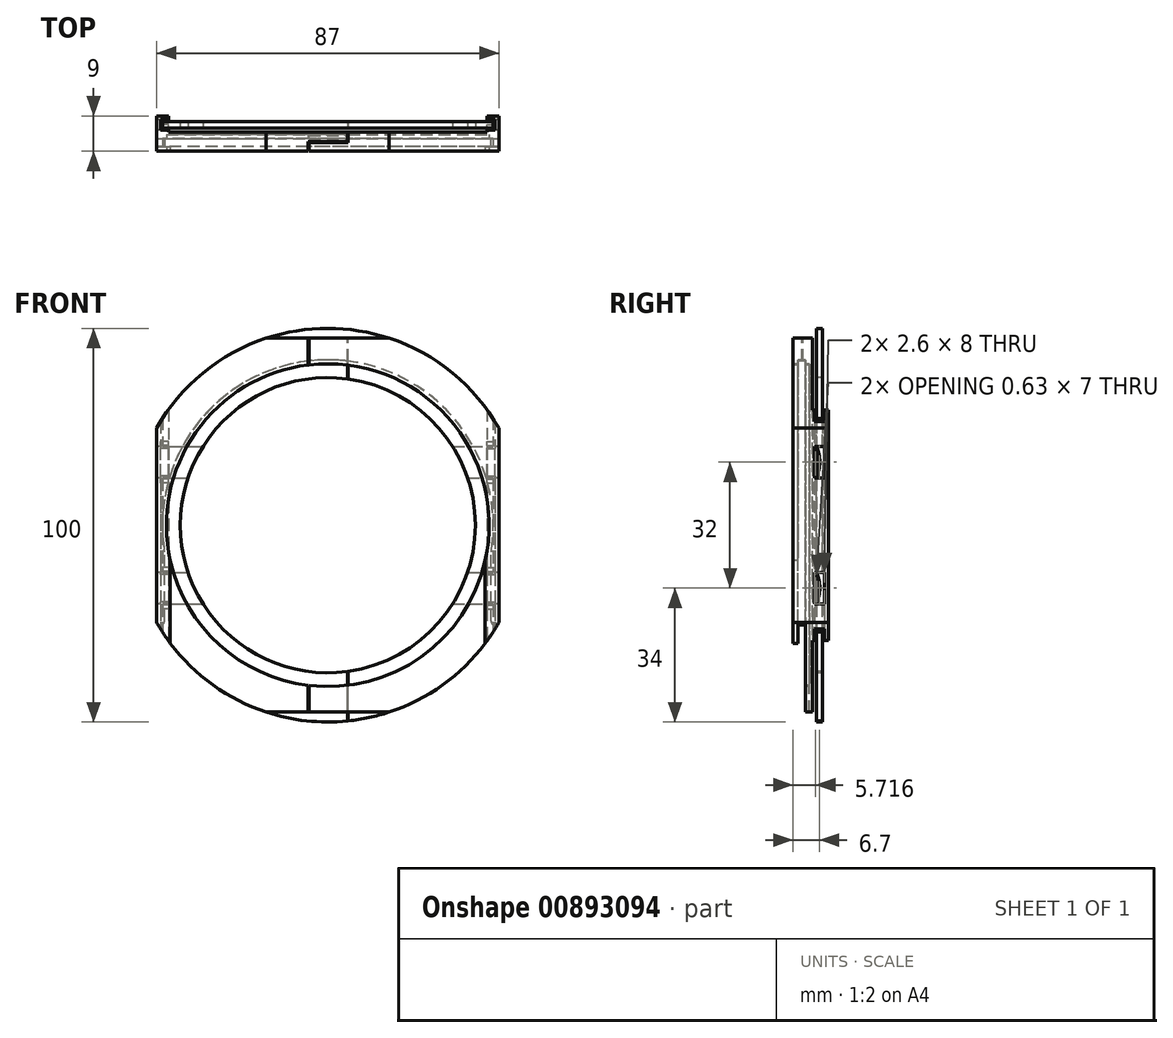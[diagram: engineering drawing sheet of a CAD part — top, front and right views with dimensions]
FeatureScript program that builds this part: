
annotation { "Feature Type Name" : "Feature", "Feature Type Description" : "" }
export const myFeature = defineFeature(function(context is Context, id is Id, definition is map)
    precondition{}
    {
        {
            var Q0;
            Q0=qCreatedBy(makeId("Front.planeOp"),FACE);
            var sketch = newSketch(context, id + "F0", { "sketchPlane" : qUnion([Q0])});
            skLineSegment(sketch, "E0.bottom", {"start": v(42, 50) * mm, "end": v(-42, 50) * mm});
            skLineSegment(sketch, "E0.top", {"start": v(42, -50) * mm, "end": v(-42, -50) * mm});
            skLineSegment(sketch, "E0.left", {"start": v(42, 50) * mm, "end": v(42, -50) * mm});
            skLineSegment(sketch, "E0.right", {"start": v(-42, 50) * mm, "end": v(-42, -50) * mm});
            skPoint(sketch, "E0.middle", {"position": v(0, 0) * mm});
            skSolve(sketch);
        }
        {
            var Q0;
            Q0=makeQuery(id+"F0.imprint","IMPRINT",FACE,{"disambiguationData":[TD([[makeQuery(id+"F0.imprint","IMPRINT",EDGE,{"derivedFrom":sQuery(id+"F0.wireOp",EDGE,"E0.bottom")}),1.0]])]});
            extrude(context, id + "F1", {"entities" : qUnion([Q0]), "depth" : .8 * mm, "offsetDistance" : 25 * mm, "hasSecondDirection" : true, "secondDirectionOppositeDirection" : true, "secondDirectionDepth" : .8 * mm});
        }
        {
            var Q0;
            Q0=qCreatedBy(makeId("Top.planeOp"),FACE);
            var sketch = newSketch(context, id + "F2", { "sketchPlane" : qUnion([Q0])});
            skLineSegment(sketch, "E1.0", {"start": v(42, 0.8) * mm, "end": v(-42, 0.8) * mm, "construction": true});
            skLineSegment(sketch, "E2.0", {"start": v(-42, -0.8) * mm, "end": v(-42, 0.8) * mm, "construction": true});
            skLineSegment(sketch, "E3.0", {"start": v(42, -0.8) * mm, "end": v(-42, -0.8) * mm, "construction": true});
            skLineSegment(sketch, "E4.0", {"start": v(42, -0.8) * mm, "end": v(42, 0.8) * mm, "construction": true});
            skLineSegment(sketch, "E5", {"start": v(-42.5, 1.3) * mm, "end": v(-42.5, -1.3) * mm});
            skLineSegment(sketch, "E6", {"start": v(-42.5, 1.3) * mm, "end": v(-40.5, 1.3) * mm});
            skLineSegment(sketch, "E7.MirrorCS", {"start": v(42.5, 1.3) * mm, "end": v(42.5, -1.3) * mm});
            skLineSegment(sketch, "E8.MirrorCS", {"start": v(42.5, 1.3) * mm, "end": v(40.5, 1.3) * mm});
            skLineSegment(sketch, "E9", {"start": v(-40.5, 1.3) * mm, "end": v(-40.5, 2.3) * mm});
            skLineSegment(sketch, "E10", {"start": v(-40.5, 2.3) * mm, "end": v(-43.5, 2.3) * mm});
            skLineSegment(sketch, "E11", {"start": v(-43.5, 2.3) * mm, "end": v(-43.5, -6.7) * mm});
            skLineSegment(sketch, "E12.MirrorCS", {"start": v(40.5, 1.3) * mm, "end": v(40.5, 2.3) * mm});
            skLineSegment(sketch, "E13.MirrorCS", {"start": v(40.5, 2.3) * mm, "end": v(43.5, 2.3) * mm});
            skLineSegment(sketch, "E14.MirrorCS", {"start": v(43.5, 2.3) * mm, "end": v(43.5, -6.7) * mm});
            skLineSegment(sketch, "E15", {"start": v(-43.5, -6.7) * mm, "end": v(43.5, -6.7) * mm});
            skLineSegment(sketch, "E16", {"start": v(-42.5, -1.3) * mm, "end": v(-40.5, -1.3) * mm});
            skLineSegment(sketch, "E17", {"start": v(-40.5, -1.3) * mm, "end": v(-40.5, -1.8) * mm});
            skLineSegment(sketch, "E18.MirrorCS", {"start": v(42.5, -1.3) * mm, "end": v(40.5, -1.3) * mm});
            skLineSegment(sketch, "E19.MirrorCS", {"start": v(40.5, -1.3) * mm, "end": v(40.5, -1.8) * mm});
            skLineSegment(sketch, "E20", {"start": v(40.5, -1.8) * mm, "end": v(-40.5, -1.8) * mm});
            skSolve(sketch);
        }
        {
            var Q0;
            Q0=qSketchRegion(id+"F2",true);
            extrude(context, id + "F3", {"entities" : qUnion([Q0]), "endBound" : BoundingType.SYMMETRIC, "depth" : 95 * mm, "offsetDistance" : 25 * mm});
        }
        {
            var Q0;
            Q0=qCreatedBy(makeId("Right.planeOp"),FACE);
            var sketch = newSketch(context, id + "F4", { "sketchPlane" : qUnion([Q0])});
            skLineSegment(sketch, "E21.top", {"start": v(3, 37.5) * mm, "end": v(-2.5, 37.5) * mm});
            skLineSegment(sketch, "E22", {"start": v(-2.5, 37.5) * mm, "end": v(-2.5, 41) * mm});
            skLineSegment(sketch, "E23", {"start": v(-2.5, 41) * mm, "end": v(-3.5, 41) * mm});
            skLineSegment(sketch, "E24", {"start": v(-3.5, 41) * mm, "end": v(-3.5, 42) * mm});
            skLineSegment(sketch, "E25", {"start": v(-3.5, 42) * mm, "end": v(-5.5, 42) * mm});
            skLineSegment(sketch, "E26", {"start": v(-5.5, 42) * mm, "end": v(-5.5, 41) * mm});
            skLineSegment(sketch, "E27", {"start": v(-5.5, 41) * mm, "end": v(-7.5, 41) * mm});
            skLineSegment(sketch, "E28", {"start": v(-7.5, 41) * mm, "end": v(-7.5, 0) * mm});
            skLineSegment(sketch, "E29", {"start": v(3, 37.5) * mm, "end": v(3, 0) * mm});
            skLineSegment(sketch, "E30", {"start": v(3, 0) * mm, "end": v(-7.5, 0) * mm});
            skSolve(sketch);
        }
        {
            var Q0;
            Q0=qSketchRegion(id+"F4",true);
            var Q1;
            Q1=sQuery(id+"F4.wireOp",EDGE,"E30");
            revolve(context, id + "F5", {"operationType" : NewBodyOperationType.REMOVE, "surfaceOperationType" : NewSurfaceOperationType.NEW, "entities" : qUnion([Q0]), "axis" : qUnion([Q1]), "revolveType" : RevolveType.FULL, "oppositeDirection" : true});
        }
        {
            var Q0;
            Q0=makeQuery(id+"F3.opExtrude","SWEPT_FACE",FACE,{"disambiguationData":[OSD([sQuery(id+"F2.wireOp",EDGE,"E15")])]});
            var sketch = newSketch(context, id + "F6", { "sketchPlane" : qUnion([Q0])});
            skLineSegment(sketch, "E31.0.0", {"start": v(-43.5, -47.5) * mm, "end": v(43.5, -47.5) * mm, "construction": true});
            skLineSegment(sketch, "E31.0.1", {"start": v(43.5, -47.5) * mm, "end": v(43.5, 47.5) * mm, "construction": true});
            skLineSegment(sketch, "E31.0.2", {"start": v(43.5, 47.5) * mm, "end": v(-43.5, 47.5) * mm, "construction": true});
            skLineSegment(sketch, "E31.0.3", {"start": v(-43.5, 47.5) * mm, "end": v(-43.5, -47.5) * mm, "construction": true});
            skLineSegment(sketch, "E32", {"start": v(-40, -9) * mm, "end": v(-40, -47.5) * mm});
            skLineSegment(sketch, "E33", {"start": v(40, -9) * mm, "end": v(40, -47.5) * mm});
            skArc(sketch, "E34", {"start": v(-40, -9) * mm, "mid": v(0, -41) * mm, "end": v(40, -9) * mm});
            skLineSegment(sketch, "E35", {"start": v(-40, -47.5) * mm, "end": v(40, -47.5) * mm});
            skSolve(sketch);
        }
        {
            var Q0;
            Q0=qSketchRegion(id+"F6",true);
            var Q1;
            Q1=makeQuery(id+"F5.boolean.opBoolean","COPY",FACE,{"derivedFrom":makeQuery(id+"F5.opRevolve","SWEPT_FACE",FACE,{"disambiguationData":[OSD([sQuery(id+"F4.wireOp",EDGE,"E24")])]})});
            extrude(context, id + "F7", {"entities" : qUnion([Q0]), "operationType" : NewBodyOperationType.REMOVE, "endBound" : BoundingType.UP_TO_SURFACE, "oppositeDirection" : true, "depth" : 25 * mm, "endBoundEntityFace" : qUnion([Q1]), "offsetDistance" : 25 * mm});
        }
        {
            var Q0;
            Q0=qCreatedBy(makeId("Front.planeOp"),FACE);
            var sketch = newSketch(context, id + "F8", { "sketchPlane" : qUnion([Q0])});
            skCircle(sketch, "E36", {"center": v(0, 0) * mm, "radius": 50 * mm});
            skCircle(sketch, "E37", {"center": v(0, 0) * mm, "radius": 70 * mm});
            skSolve(sketch);
        }
        {
            var Q0;
            Q0=qSketchRegion(id+"F8",true);
            extrude(context, id + "F9", {"entities" : qUnion([Q0]), "operationType" : NewBodyOperationType.REMOVE, "endBound" : BoundingType.SYMMETRIC, "oppositeDirection" : true, "depth" : 500 * mm, "offsetDistance" : 25 * mm});
        }
        {
            var Q0;
            Q0=qCreatedBy(makeId("Top.planeOp"),FACE);
            var sketch = newSketch(context, id + "F10", { "sketchPlane" : qUnion([Q0])});
            skLineSegment(sketch, "E38.0", {"start": v(41, -5.5) * mm, "end": v(-41, -5.5) * mm, "construction": true});
            skLineSegment(sketch, "E39", {"start": v(-42, -4.5) * mm, "end": v(-42, -3.5) * mm, "construction": true});
            skLineSegment(sketch, "E40", {"start": v(42, -3.5) * mm, "end": v(42, -4.5) * mm, "construction": true});
            skLineSegment(sketch, "E41.bottom", {"start": v(-41.5, -5.5) * mm, "end": v(41.5, -5.5) * mm});
            skLineSegment(sketch, "E41.top", {"start": v(-41.5, -3.5) * mm, "end": v(41.5, -3.5) * mm});
            skLineSegment(sketch, "E41.left", {"start": v(-41.5, -5.5) * mm, "end": v(-41.5, -3.5) * mm});
            skLineSegment(sketch, "E41.right", {"start": v(41.5, -5.5) * mm, "end": v(41.5, -3.5) * mm});
            skSolve(sketch);
        }
        {
            var Q0;
            Q0=qSketchRegion(id+"F10",true);
            extrude(context, id + "F11", {"entities" : qUnion([Q0]), "operationType" : NewBodyOperationType.REMOVE, "oppositeDirection" : true, "depth" : 50 * mm, "offsetDistance" : 25 * mm});
        }
        {
            var Q0;
            Q0=makeQuery(id+"F11.boolean.opBoolean","INTERSECT",EDGE,{"derivedFrom":[makeQuery(id+"F5.boolean.opBoolean","COPY",FACE,{"derivedFrom":makeQuery(id+"F5.opRevolve","SWEPT_FACE",FACE,{"disambiguationData":[OSD([sQuery(id+"F4.wireOp",EDGE,"E25")])]})}),makeQuery(id+"F11.opExtrude","SWEPT_FACE",FACE,{"disambiguationData":[OSD([sQuery(id+"F10.wireOp",EDGE,"E41.right")])]})]});
            var Q1;
            Q1=makeQuery(id+"F11.boolean.opBoolean","INTERSECT",EDGE,{"derivedFrom":[makeQuery(id+"F5.boolean.opBoolean","COPY",FACE,{"derivedFrom":makeQuery(id+"F5.opRevolve","SWEPT_FACE",FACE,{"disambiguationData":[OSD([sQuery(id+"F4.wireOp",EDGE,"E25")])]})}),makeQuery(id+"F11.opExtrude","SWEPT_FACE",FACE,{"disambiguationData":[OSD([sQuery(id+"F10.wireOp",EDGE,"E41.left")])]})]});
            fillet(context, id + "F12", {"entities" : qUnion([Q0, Q1]), "radius" : 5 * mm, "tangentPropagation" : true, "allowEdgeOverflow" : false});
        }
        {
            var Q0;
            {var subQ0=sQuery(id+"F2.wireOp",EDGE,"E16");var subQ1=sQuery(id+"F2.wireOp",EDGE,"E11");var subQ2=sQuery(id+"F2.wireOp",EDGE,"E10");var subQ3=sQuery(id+"F2.wireOp",EDGE,"E5");var subQ4=sQuery(id+"F2.wireOp",EDGE,"E15");var subQ5=sQuery(id+"F2.wireOp",EDGE,"E20");var subQ6=sQuery(id+"F2.wireOp",EDGE,"E17");var subQ7=sQuery(id+"F2.wireOp",EDGE,"E9");var subQ8=sQuery(id+"F2.wireOp",EDGE,"E6");Q0=makeQuery(id+"F11.boolean.opBoolean","INTERSECT",EDGE,{"derivedFrom":[makeQuery(id+"F9.boolean.opBoolean","COPY",FACE,{"disambiguationData":[TD([makeQuery(id+"F3.opExtrude","SWEPT_FACE",FACE,{"disambiguationData":[OSD([subQ3])]}),makeQuery(id+"F3.opExtrude","CAP_FACE",FACE,{"disambiguationData":[OSD([subQ3,subQ8,sQuery(id+"F2.wireOp",EDGE,"E7.MirrorCS"),sQuery(id+"F2.wireOp",EDGE,"E8.MirrorCS"),subQ7,subQ2,subQ1,sQuery(id+"F2.wireOp",EDGE,"E12.MirrorCS"),sQuery(id+"F2.wireOp",EDGE,"E13.MirrorCS"),sQuery(id+"F2.wireOp",EDGE,"E14.MirrorCS"),subQ4,subQ0,subQ6,sQuery(id+"F2.wireOp",EDGE,"E18.MirrorCS"),sQuery(id+"F2.wireOp",EDGE,"E19.MirrorCS"),subQ5])],"isStart":true}),makeQuery(id+"F3.opExtrude","SWEPT_FACE",FACE,{"disambiguationData":[OSD([subQ8])]}),makeQuery(id+"F3.opExtrude","SWEPT_FACE",FACE,{"disambiguationData":[OSD([subQ7])]}),makeQuery(id+"F3.opExtrude","SWEPT_FACE",FACE,{"disambiguationData":[OSD([subQ2])]}),makeQuery(id+"F3.opExtrude","SWEPT_FACE",FACE,{"disambiguationData":[OSD([subQ1])]}),makeQuery(id+"F3.opExtrude","SWEPT_FACE",FACE,{"disambiguationData":[OSD([subQ4])]}),makeQuery(id+"F3.opExtrude","SWEPT_FACE",FACE,{"disambiguationData":[OSD([subQ0])]}),makeQuery(id+"F3.opExtrude","SWEPT_FACE",FACE,{"disambiguationData":[OSD([subQ6])]}),makeQuery(id+"F3.opExtrude","SWEPT_FACE",FACE,{"disambiguationData":[OSD([subQ5])]}),makeQuery(id+"F5.boolean.opBoolean","COPY",FACE,{"derivedFrom":makeQuery(id+"F5.opRevolve","SWEPT_FACE",FACE,{"disambiguationData":[OSD([sQuery(id+"F4.wireOp",EDGE,"E24")])]})}),makeQuery(id+"F7.boolean.opBoolean","COPY",FACE,{"derivedFrom":makeQuery(id+"F7.opExtrude","SWEPT_FACE",FACE,{"disambiguationData":[OSD([sQuery(id+"F6.wireOp",EDGE,"E32")])]})})])],"derivedFrom":makeQuery(id+"F9.opExtrude","SWEPT_FACE",FACE,{"disambiguationData":[OSD([sQuery(id+"F8.wireOp",EDGE,"E36")])]})}),makeQuery(id+"F11.opExtrude","SWEPT_FACE",FACE,{"disambiguationData":[OSD([sQuery(id+"F10.wireOp",EDGE,"E41.left")])]})]});}
            var Q1;
            {var subQ0=sQuery(id+"F2.wireOp",EDGE,"E20");var subQ1=sQuery(id+"F2.wireOp",EDGE,"E14.MirrorCS");var subQ2=sQuery(id+"F2.wireOp",EDGE,"E13.MirrorCS");var subQ3=sQuery(id+"F2.wireOp",EDGE,"E15");var subQ4=sQuery(id+"F2.wireOp",EDGE,"E19.MirrorCS");var subQ5=sQuery(id+"F2.wireOp",EDGE,"E18.MirrorCS");var subQ6=sQuery(id+"F2.wireOp",EDGE,"E12.MirrorCS");var subQ7=sQuery(id+"F2.wireOp",EDGE,"E8.MirrorCS");var subQ8=sQuery(id+"F2.wireOp",EDGE,"E7.MirrorCS");Q1=makeQuery(id+"F11.boolean.opBoolean","INTERSECT",EDGE,{"derivedFrom":[makeQuery(id+"F9.boolean.opBoolean","COPY",FACE,{"disambiguationData":[TD([makeQuery(id+"F3.opExtrude","CAP_FACE",FACE,{"disambiguationData":[OSD([sQuery(id+"F2.wireOp",EDGE,"E5"),sQuery(id+"F2.wireOp",EDGE,"E6"),subQ8,subQ7,sQuery(id+"F2.wireOp",EDGE,"E9"),sQuery(id+"F2.wireOp",EDGE,"E10"),sQuery(id+"F2.wireOp",EDGE,"E11"),subQ6,subQ2,subQ1,subQ3,sQuery(id+"F2.wireOp",EDGE,"E16"),sQuery(id+"F2.wireOp",EDGE,"E17"),subQ5,subQ4,subQ0])],"isStart":true}),makeQuery(id+"F3.opExtrude","SWEPT_FACE",FACE,{"disambiguationData":[OSD([subQ8])]}),makeQuery(id+"F3.opExtrude","SWEPT_FACE",FACE,{"disambiguationData":[OSD([subQ7])]}),makeQuery(id+"F3.opExtrude","SWEPT_FACE",FACE,{"disambiguationData":[OSD([subQ6])]}),makeQuery(id+"F3.opExtrude","SWEPT_FACE",FACE,{"disambiguationData":[OSD([subQ2])]}),makeQuery(id+"F3.opExtrude","SWEPT_FACE",FACE,{"disambiguationData":[OSD([subQ1])]}),makeQuery(id+"F3.opExtrude","SWEPT_FACE",FACE,{"disambiguationData":[OSD([subQ3])]}),makeQuery(id+"F3.opExtrude","SWEPT_FACE",FACE,{"disambiguationData":[OSD([subQ5])]}),makeQuery(id+"F3.opExtrude","SWEPT_FACE",FACE,{"disambiguationData":[OSD([subQ4])]}),makeQuery(id+"F3.opExtrude","SWEPT_FACE",FACE,{"disambiguationData":[OSD([subQ0])]}),makeQuery(id+"F5.boolean.opBoolean","COPY",FACE,{"derivedFrom":makeQuery(id+"F5.opRevolve","SWEPT_FACE",FACE,{"disambiguationData":[OSD([sQuery(id+"F4.wireOp",EDGE,"E24")])]})}),makeQuery(id+"F7.boolean.opBoolean","COPY",FACE,{"derivedFrom":makeQuery(id+"F7.opExtrude","SWEPT_FACE",FACE,{"disambiguationData":[OSD([sQuery(id+"F6.wireOp",EDGE,"E33")])]})})])],"derivedFrom":makeQuery(id+"F9.opExtrude","SWEPT_FACE",FACE,{"disambiguationData":[OSD([sQuery(id+"F8.wireOp",EDGE,"E36")])]})}),makeQuery(id+"F11.opExtrude","SWEPT_FACE",FACE,{"disambiguationData":[OSD([sQuery(id+"F10.wireOp",EDGE,"E41.right")])]})]});}
            fillet(context, id + "F13", {"entities" : qUnion([Q0, Q1]), "radius" : 1 * mm, "tangentPropagation" : true, "allowEdgeOverflow" : false});
        }
        {
            var Q0;
            Q0=qCreatedBy(makeId("Right.planeOp"),FACE);
            var sketch = newSketch(context, id + "F14", { "sketchPlane" : qUnion([Q0])});
            skLineSegment(sketch, "E42.0.0", {"start": v(-6.7, 24.65) * mm, "end": v(2.3, 24.65) * mm, "construction": true});
            skLineSegment(sketch, "E42.0.1", {"start": v(2.3, 24.65) * mm, "end": v(2.3, -24.65) * mm, "construction": true});
            skLineSegment(sketch, "E42.0.2", {"start": v(-6.7, -24.65) * mm, "end": v(2.3, -24.65) * mm, "construction": true});
            skLineSegment(sketch, "E42.0.3", {"start": v(-6.7, -24.65) * mm, "end": v(-6.7, 24.65) * mm, "construction": true});
            skLineSegment(sketch, "E43.0", {"start": v(1.3, 26.34) * mm, "end": v(-1.3, 26.34) * mm, "construction": true});
            skLineSegment(sketch, "E44.0", {"start": v(-1.3, -26.34) * mm, "end": v(1.3, -26.34) * mm, "construction": true});
            skLineSegment(sketch, "E45.bottom", {"start": v(1.3, 20) * mm, "end": v(-1.3, 20) * mm});
            skLineSegment(sketch, "E45.top", {"start": v(1.3, 12) * mm, "end": v(-1.3, 12) * mm});
            skLineSegment(sketch, "E45.left", {"start": v(1.3, 20) * mm, "end": v(1.3, 12) * mm});
            skLineSegment(sketch, "E45.right", {"start": v(-1.3, 20) * mm, "end": v(-1.3, 12) * mm});
            skLineSegment(sketch, "E46.MirrorCS", {"start": v(1.3, -20) * mm, "end": v(-1.3, -20) * mm});
            skLineSegment(sketch, "E47.MirrorCS", {"start": v(-1.3, -20) * mm, "end": v(-1.3, -12) * mm});
            skLineSegment(sketch, "E48.MirrorCS", {"start": v(1.3, -12) * mm, "end": v(-1.3, -12) * mm});
            skLineSegment(sketch, "E49.MirrorCS", {"start": v(1.3, -20) * mm, "end": v(1.3, -12) * mm});
            skSolve(sketch);
        }
        {
            var Q0;
            Q0=makeQuery(id+"F14.imprint","IMPRINT",FACE,{"disambiguationData":[TD([[makeQuery(id+"F14.imprint","IMPRINT",EDGE,{"derivedFrom":sQuery(id+"F14.wireOp",EDGE,"E45.bottom")}),1.0]])]});
            var Q1;
            Q1=makeQuery(id+"F14.imprint","IMPRINT",FACE,{"disambiguationData":[TD([[makeQuery(id+"F14.imprint","IMPRINT",EDGE,{"derivedFrom":sQuery(id+"F14.wireOp",EDGE,"E46.MirrorCS")}),-1.0]])]});
            extrude(context, id + "F15", {"entities" : qUnion([Q0, Q1]), "operationType" : NewBodyOperationType.REMOVE, "endBound" : BoundingType.SYMMETRIC, "depth" : 100 * mm, "offsetDistance" : 25 * mm});
        }
        {
            var Q0;
            Q0=makeQuery(id+"F15.boolean.opBoolean","SPLIT",FACE,{"disambiguationData":[TD([makeQuery(id+"F15.opExtrude","SWEPT_FACE",FACE,{"disambiguationData":[OSD([sQuery(id+"F14.wireOp",EDGE,"E45.top")])]})])],"derivedFrom":makeQuery(id+"F3.opExtrude","SWEPT_FACE",FACE,{"disambiguationData":[OSD([sQuery(id+"F2.wireOp",EDGE,"E5")])]})});
            var sketch = newSketch(context, id + "F16", { "sketchPlane" : qUnion([Q0])});
            skLineSegment(sketch, "E50.0", {"start": v(-1.3, 20) * mm, "end": v(1.3, 20) * mm, "construction": true});
            skLineSegment(sketch, "E51.0", {"start": v(-1.3, 12) * mm, "end": v(1.3, 12) * mm, "construction": true});
            skArc(sketch, "E52", {"start": v(-1.3, 12.5) * mm, "mid": v(-0.67, 16) * mm, "end": v(-1.3, 19.5) * mm});
            skLineSegment(sketch, "E53", {"start": v(-1.55, 21.66) * mm, "end": v(-1.55, 9.87) * mm});
            skLineSegment(sketch, "E54", {"start": v(6.42, 16) * mm, "end": v(-9.93, 16) * mm, "construction": true});
            skArc(sketch, "E55.0", {"start": v(-1.3, 10.73) * mm, "mid": v(0.08, 16) * mm, "end": v(-1.3, 21.27) * mm});
            skLineSegment(sketch, "E56", {"start": v(-1.3, 21.27) * mm, "end": v(-1.3, 19.5) * mm});
            skLineSegment(sketch, "E57", {"start": v(-1.3, 12.5) * mm, "end": v(-1.3, 10.73) * mm});
            skSolve(sketch);
        }
        {
            var Q0;
            {var subQ0=sQuery(id+"F16.wireOp",EDGE,"E56");Q0=makeQuery(id+"F16.imprint","IMPRINT",FACE,{"disambiguationData":[TD([[makeQuery(id+"F16.imprint","IMPRINT",EDGE,{"derivedFrom":subQ0}),1.0]])]});}
            var Q1;
            {var subQ0=sQuery(id+"F16.wireOp",EDGE,"E57");Q1=makeQuery(id+"F16.imprint","IMPRINT",FACE,{"disambiguationData":[TD([[makeQuery(id+"F16.imprint","IMPRINT",EDGE,{"derivedFrom":subQ0}),1.0]])]});}
            extrude(context, id + "F17", {"entities" : qUnion([Q0, Q1]), "depth" : 2 * mm, "offsetDistance" : 25 * mm});
        }
        {
            var Q0;
            Q0=makeQuery(id+"F17.opExtrude","SWEPT_BODY",BODY,{"disambiguationData":[OSD([sQuery(id+"F16.wireOp",EDGE,"E52"),sQuery(id+"F16.wireOp",EDGE,"E55.0"),sQuery(id+"F16.wireOp",EDGE,"E56"),sQuery(id+"F16.wireOp",EDGE,"E57")])]});
            var Q1;
            Q1=qCreatedBy(makeId("Right.planeOp"),FACE);
            mirror(context, id + "F18", {"entities" : qUnion([Q0]), "mirrorPlane" : qUnion([Q1])});
        }
        {
            var Q0;
            Q0=makeQuery(id+"F18.opPattern","COPY",BODY,{"derivedFrom":makeQuery(id+"F17.opExtrude","SWEPT_BODY",BODY,{"disambiguationData":[OSD([sQuery(id+"F16.wireOp",EDGE,"E52"),sQuery(id+"F16.wireOp",EDGE,"E55.0"),sQuery(id+"F16.wireOp",EDGE,"E56"),sQuery(id+"F16.wireOp",EDGE,"E57")])]}),"instanceName":"1"});
            var Q1;
            Q1=makeQuery(id+"F17.opExtrude","SWEPT_BODY",BODY,{"disambiguationData":[OSD([sQuery(id+"F16.wireOp",EDGE,"E52"),sQuery(id+"F16.wireOp",EDGE,"E55.0"),sQuery(id+"F16.wireOp",EDGE,"E56"),sQuery(id+"F16.wireOp",EDGE,"E57")])]});
            var Q2;
            Q2=qCreatedBy(makeId("Top.planeOp"),FACE);
            mirror(context, id + "F19", {"operationType" : NewBodyOperationType.ADD, "entities" : qUnion([Q0, Q1]), "mirrorPlane" : qUnion([Q2])});
        }
        {
            var Q0;
            Q0=qCreatedBy(makeId("Top.planeOp"),FACE);
            var sketch = newSketch(context, id + "F20", { "sketchPlane" : qUnion([Q0])});
            skLineSegment(sketch, "E58", {"start": v(-5, -14.33) * mm, "end": v(-5, -2.5) * mm});
            skLineSegment(sketch, "E59", {"start": v(-5, -2.5) * mm, "end": v(5, -2.5) * mm});
            skLineSegment(sketch, "E60", {"start": v(5, -2.5) * mm, "end": v(5, 12.35) * mm});
            skLineSegment(sketch, "E61.0", {"start": v(5.2, -2.7) * mm, "end": v(5.2, 12.35) * mm});
            skLineSegment(sketch, "E61.1", {"start": v(-4.8, -2.7) * mm, "end": v(5.2, -2.7) * mm});
            skLineSegment(sketch, "E61.2", {"start": v(-4.8, -14.33) * mm, "end": v(-4.8, -2.7) * mm});
            skLineSegment(sketch, "E62", {"start": v(-5, -14.33) * mm, "end": v(-4.8, -14.33) * mm});
            skLineSegment(sketch, "E63", {"start": v(5, 12.35) * mm, "end": v(5.2, 12.35) * mm});
            skSolve(sketch);
        }
        {
            var Q0;
            Q0 = qSketchRegion(id + "F20", true);
            extrude(context, id + "F21", {"entities" : qUnion([Q0]), "operationType" : NewBodyOperationType.REMOVE, "endBound" : BoundingType.THROUGH_ALL, "oppositeDirection" : true, "depth" : 25 * mm, "offsetDistance" : 25 * mm});
        }
        {
            var Q0;
            Q0=makeQuery(id+"F3.opExtrude","CAP_FACE",FACE,{"disambiguationData":[OSD([sQuery(id+"F2.wireOp",EDGE,"E5"),sQuery(id+"F2.wireOp",EDGE,"E6"),sQuery(id+"F2.wireOp",EDGE,"E7.MirrorCS"),sQuery(id+"F2.wireOp",EDGE,"E8.MirrorCS"),sQuery(id+"F2.wireOp",EDGE,"E9"),sQuery(id+"F2.wireOp",EDGE,"E10"),sQuery(id+"F2.wireOp",EDGE,"E11"),sQuery(id+"F2.wireOp",EDGE,"E12.MirrorCS"),sQuery(id+"F2.wireOp",EDGE,"E13.MirrorCS"),sQuery(id+"F2.wireOp",EDGE,"E14.MirrorCS"),sQuery(id+"F2.wireOp",EDGE,"E15"),sQuery(id+"F2.wireOp",EDGE,"E16"),sQuery(id+"F2.wireOp",EDGE,"E17"),sQuery(id+"F2.wireOp",EDGE,"E18.MirrorCS"),sQuery(id+"F2.wireOp",EDGE,"E19.MirrorCS"),sQuery(id+"F2.wireOp",EDGE,"E20")])],"isStart":false});
            var sketch = newSketch(context, id + "F22", { "sketchPlane" : qUnion([Q0])});
            skLineSegment(sketch, "E64", {"start": v(-5, -6.7) * mm, "end": v(-5, -4.25) * mm});
            skLineSegment(sketch, "E65", {"start": v(-5, -4.25) * mm, "end": v(5, -4.25) * mm});
            skLineSegment(sketch, "E66", {"start": v(5, -4.25) * mm, "end": v(5, -1.8) * mm});
            skLineSegment(sketch, "E67", {"start": v(0, -5.4) * mm, "end": v(0, -6.7) * mm, "construction": true});
            skLineSegment(sketch, "E68", {"start": v(16.93, -1.8) * mm, "end": v(16.93, -6.7) * mm, "construction": true});
            skLineSegment(sketch, "E69", {"start": v(5, -4.25) * mm, "end": v(16.93, -4.25) * mm, "construction": true});
            skLineSegment(sketch, "E70.0", {"start": v(5.2, -4.45) * mm, "end": v(5.2, -1.8) * mm});
            skLineSegment(sketch, "E70.1", {"start": v(-4.8, -4.45) * mm, "end": v(5.2, -4.45) * mm});
            skLineSegment(sketch, "E70.2", {"start": v(-4.8, -6.7) * mm, "end": v(-4.8, -4.45) * mm});
            skLineSegment(sketch, "E71", {"start": v(-5, -6.7) * mm, "end": v(-4.8, -6.7) * mm});
            skLineSegment(sketch, "E72", {"start": v(5.2, -1.8) * mm, "end": v(5, -1.8) * mm});
            skSolve(sketch);
        }
        {
            var Q0;
            Q0 = qSketchRegion(id + "F22", true);
            extrude(context, id + "F23", {"entities" : qUnion([Q0]), "operationType" : NewBodyOperationType.REMOVE, "oppositeDirection" : true, "depth" : 30 * mm, "offsetDistance" : 25 * mm});
        }
    });
